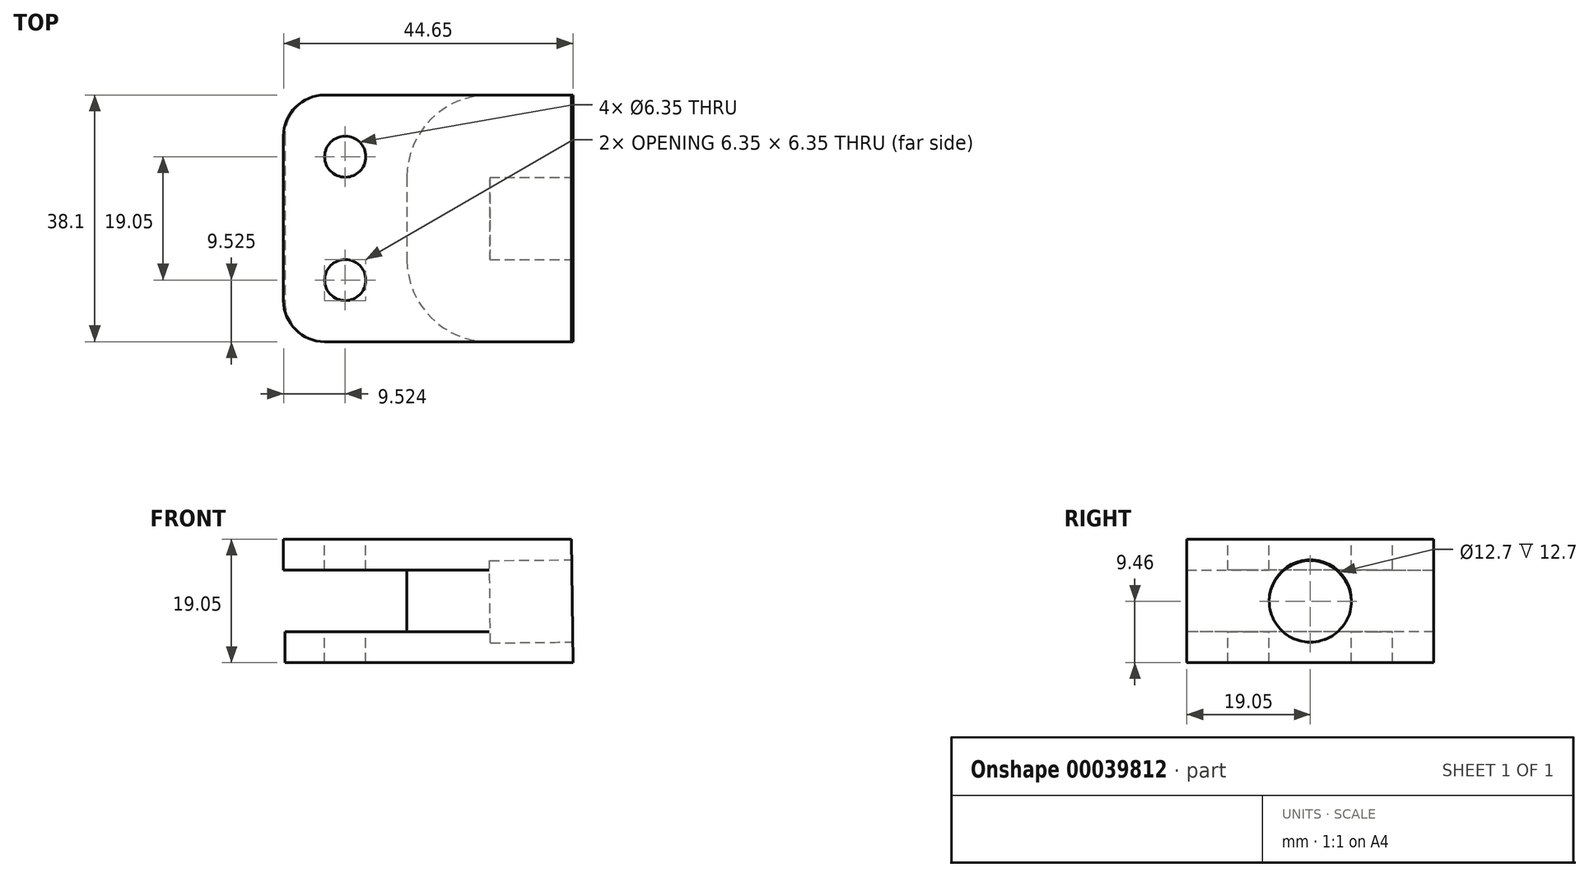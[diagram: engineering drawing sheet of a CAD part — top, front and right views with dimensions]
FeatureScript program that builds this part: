
annotation { "Feature Type Name" : "Feature", "Feature Type Description" : "" }
export const myFeature = defineFeature(function(context is Context, id is Id, definition is map)
    precondition{}
    {
        {
            var Q0;
            Q0=qCreatedBy(makeId("Front.planeOp"),FACE);
            var sketch = newSketch(context, id + "F0", { "sketchPlane" : qUnion([Q0])});
            skLineSegment(sketch, "E0", {"start": v(19.38, 22.95) * mm, "end": v(-25.07, 22.95) * mm});
            skLineSegment(sketch, "E1", {"start": v(-25.07, 22.95) * mm, "end": v(-25.07, 18.19) * mm});
            skLineSegment(sketch, "E2", {"start": v(-25.07, 18.19) * mm, "end": v(-6.02, 18.19) * mm});
            skLineSegment(sketch, "E3", {"start": v(-6.02, 18.19) * mm, "end": v(-6.02, 8.66) * mm});
            skLineSegment(sketch, "E4", {"start": v(-6.02, 8.66) * mm, "end": v(-24.87, 8.66) * mm});
            skLineSegment(sketch, "E5", {"start": v(-24.87, 8.66) * mm, "end": v(-24.87, 3.9) * mm});
            skLineSegment(sketch, "E6", {"start": v(-24.87, 3.9) * mm, "end": v(19.58, 3.9) * mm});
            skLineSegment(sketch, "E7", {"start": v(19.58, 3.9) * mm, "end": v(19.38, 22.95) * mm});
            skSolve(sketch);
        }
        {
            var Q0;
            Q0=makeQuery(id+"F0.imprint","IMPRINT",FACE,{"disambiguationData":[TD([[makeQuery(id+"F0.imprint","IMPRINT",EDGE,{"derivedFrom":sQuery(id+"F0.wireOp",EDGE,"E0")}),1.0]])]});
            extrude(context, id + "F1", {"entities" : qUnion([Q0]), "oppositeDirection" : true, "depth" : 38.1 * mm});
        }
        {
            var Q0;
            Q0=makeQuery(id+"F1.opExtrude","SWEPT_FACE",FACE,{"disambiguationData":[OSD([sQuery(id+"F0.wireOp",EDGE,"E0")])]});
            var sketch = newSketch(context, id + "F2", { "sketchPlane" : qUnion([Q0])});
            skCircle(sketch, "E8", {"center": v(-15.55, 28.58) * mm, "radius": 3.18 * mm});
            skCircle(sketch, "E9", {"center": v(-15.55, 9.52) * mm, "radius": 3.18 * mm});
            skSolve(sketch);
        }
        {
            var Q0;
            Q0=makeQuery(id+"F2.imprint","IMPRINT",FACE,{"disambiguationData":[TD([[makeQuery(id+"F2.imprint","IMPRINT",EDGE,{"derivedFrom":sQuery(id+"F2.wireOp",EDGE,"E8")}),1.0]])]});
            var Q1;
            Q1=makeQuery(id+"F2.imprint","IMPRINT",FACE,{"disambiguationData":[TD([[makeQuery(id+"F2.imprint","IMPRINT",EDGE,{"derivedFrom":sQuery(id+"F2.wireOp",EDGE,"E9")}),1.0]])]});
            extrude(context, id + "F3", {"entities" : qUnion([Q0, Q1]), "operationType" : NewBodyOperationType.REMOVE, "oppositeDirection" : true, "depth" : 25.4 * mm});
        }
        {
            var Q0;
            Q0=makeQuery(id+"F1.opExtrude","CAP_EDGE",EDGE,{"disambiguationData":[OSD([sQuery(id+"F0.wireOp",EDGE,"E1")])],"isStart":true});
            var Q1;
            Q1=makeQuery(id+"F1.opExtrude","CAP_EDGE",EDGE,{"disambiguationData":[OSD([sQuery(id+"F0.wireOp",EDGE,"E5")])],"isStart":true});
            var Q2;
            Q2=makeQuery(id+"F1.opExtrude","CAP_EDGE",EDGE,{"disambiguationData":[OSD([sQuery(id+"F0.wireOp",EDGE,"E5")])],"isStart":false});
            var Q3;
            Q3=makeQuery(id+"F1.opExtrude","CAP_EDGE",EDGE,{"disambiguationData":[OSD([sQuery(id+"F0.wireOp",EDGE,"E1")])],"isStart":false});
            fillet(context, id + "F4", {"entities" : qUnion([Q0, Q1, Q2, Q3]), "radius" : 6.35 * mm, "tangentPropagation" : true, "allowEdgeOverflow" : false});
        }
        {
            var Q0;
            Q0=makeQuery(id+"F1.opExtrude","SWEPT_FACE",FACE,{"disambiguationData":[OSD([sQuery(id+"F0.wireOp",EDGE,"E7")])]});
            var sketch = newSketch(context, id + "F5", { "sketchPlane" : qUnion([Q0])});
            skLineSegment(sketch, "E10", {"start": v(0, 13.22) * mm, "end": v(38.1, 13.22) * mm});
            skCircle(sketch, "E11", {"center": v(19.05, 13.22) * mm, "radius": 6.35 * mm});
            skSolve(sketch);
        }
        {
            var Q0;
            {var subQ0=sQuery(id+"F5.wireOp",EDGE,"E11");var subQ1=sQuery(id+"F5.wireOp",EDGE,"E10");var subQ3=makeQuery(id+"F5.imprint","INTERSECT",VERTEX,{"disambiguationData":[OD(0.0)],"derivedFrom":[subQ1,subQ0]});Q0=makeQuery(id+"F5.imprint","IMPRINT",FACE,{"disambiguationData":[TD([[makeQuery(id+"F5.imprint","IMPRINT",EDGE,{"disambiguationData":[TD([[subQ3,-1.0]])],"derivedFrom":subQ1}),1.0]])]});}
            var Q1;
            {var subQ0=sQuery(id+"F5.wireOp",EDGE,"E11");var subQ1=sQuery(id+"F5.wireOp",EDGE,"E10");var subQ3=makeQuery(id+"F5.imprint","INTERSECT",VERTEX,{"disambiguationData":[OD(0.0)],"derivedFrom":[subQ1,subQ0]});Q1=makeQuery(id+"F5.imprint","IMPRINT",FACE,{"disambiguationData":[TD([[makeQuery(id+"F5.imprint","IMPRINT",EDGE,{"disambiguationData":[TD([[subQ3,-1.0]])],"derivedFrom":subQ1}),-1.0]])]});}
            extrude(context, id + "F6", {"entities" : qUnion([Q0, Q1]), "operationType" : NewBodyOperationType.REMOVE, "oppositeDirection" : true, "depth" : 12.7 * mm});
        }
        {
            var Q0;
            Q0=makeQuery(id+"F1.opExtrude","CAP_EDGE",EDGE,{"disambiguationData":[OSD([sQuery(id+"F0.wireOp",EDGE,"E3")])],"isStart":true});
            fillet(context, id + "F7", {"entities" : qUnion([Q0]), "radius" : 12.7 * mm, "tangentPropagation" : true, "allowEdgeOverflow" : false});
        }
        {
            var Q0;
            Q0=makeQuery(id+"F1.opExtrude","CAP_EDGE",EDGE,{"disambiguationData":[OSD([sQuery(id+"F0.wireOp",EDGE,"E3")])],"isStart":false});
            fillet(context, id + "F8", {"entities" : qUnion([Q0]), "radius" : 12.7 * mm, "tangentPropagation" : true, "allowEdgeOverflow" : false});
        }
    });
